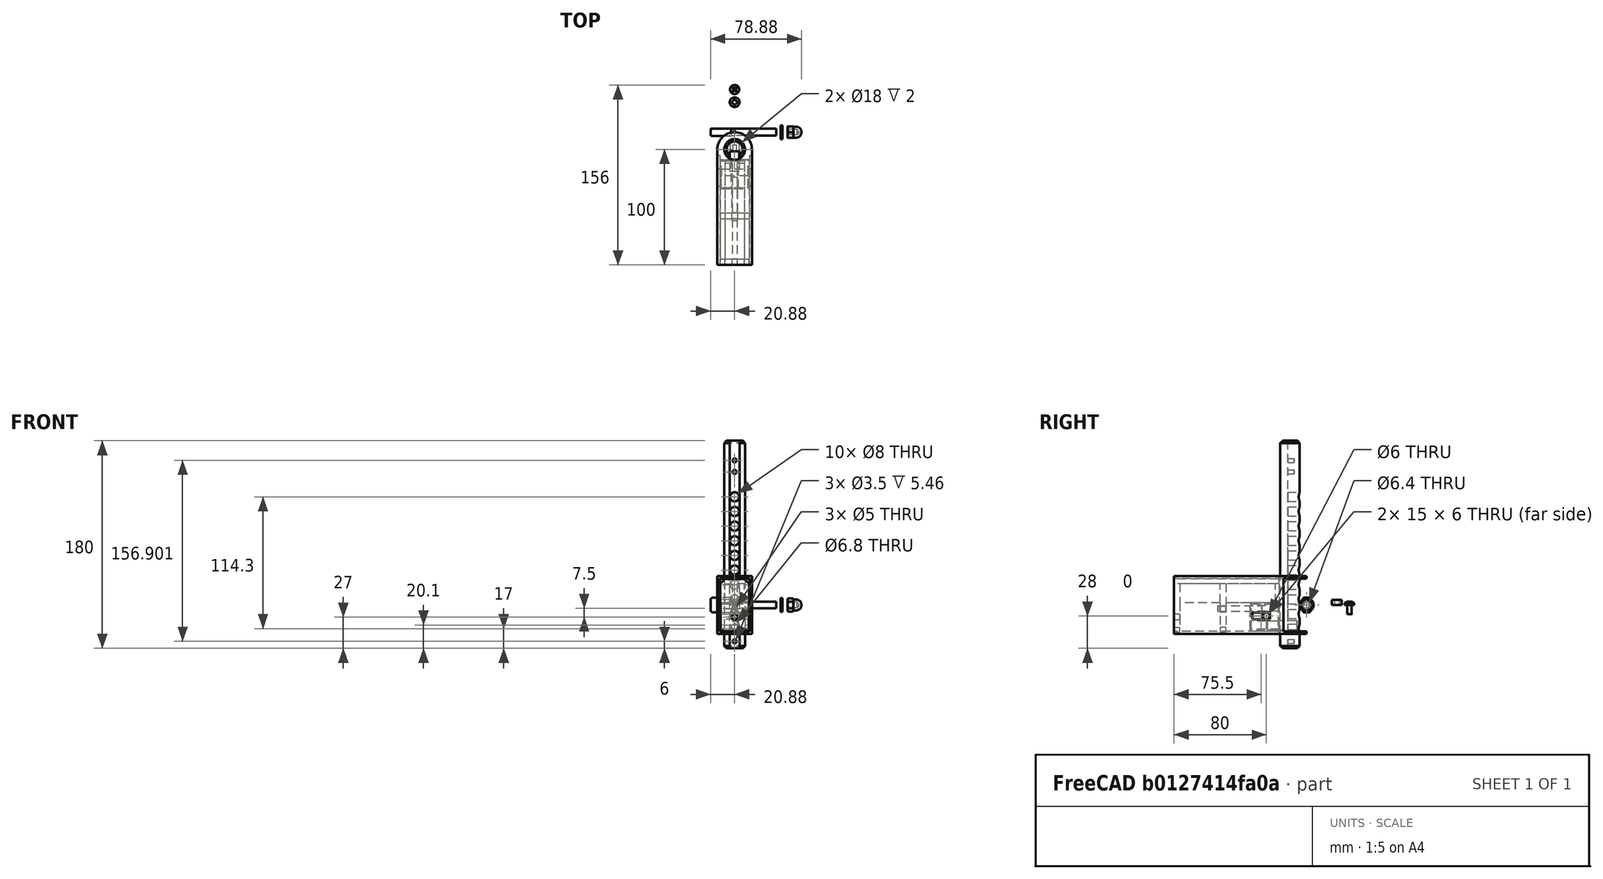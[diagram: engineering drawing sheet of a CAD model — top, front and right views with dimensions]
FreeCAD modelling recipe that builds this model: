
FCSTD DOCUMENT  (FreeCAD 0.20R29603 (Git))
Label: armrest
License: All rights reserved
LicenseURL: http://en.wikipedia.org/wiki/All_rights_reserved
objects: TechDraw::DrawViewDimension×48, Sketcher::SketchObject×21, PartDesign::Pad×13, TechDraw::DrawProjGroupItem×11, PartDesign::Pocket×8, PartDesign::Body×8, TechDraw::DrawProjGroup×6, Part::FeaturePython×3, TechDraw::DrawSVGTemplate×3, TechDraw::DrawViewAnnotation×3, TechDraw::DrawPage×3, PartDesign::Chamfer×2, PartDesign::Fillet×2, App::DocumentObjectGroup×2, Spreadsheet::Sheet×1, PartDesign::Mirrored×1, TechDraw::DrawViewDimExtent×1
note: 83 computed .brp shape members not serialized (recipe doc carries the construction recipe); baked Part::Feature solids carry a one-line shape summary decoded from their .brp

FEATURE [Spreadsheet::Sheet] Spreadsheet  label="data"
  cells = A1=rod_dia; B1(rod_dia)=18; A2=rod_length; B2(rod_length)=180; C2==25.4 * 7.25; A3=rod_angle; B3(rod_angle)=117; A4=rod_holespacing; B4(rod_holespacing)==25.4 / 2; A5=rod_holedia; B5(rod_holedia)=8; A6=rod_slotwidth; B6(rod_slotwidth)=8.4; A7=rod_slotheight; B7(rod_slotheight)=6.5; A8=rod_pindia; B8(rod_pindia)=5; A9=rod_blockerdia; B9(rod_blockerdia)=3.5; A11=body_width; B11(body_width)=30; A12=body_height; B12(body_height)=50; A13=body_walls; B13(body_walls)=2; A14=body_length; B14(body_length)=115; A16=lever_height; B16(lever_height)==25.4 / 2; A17=lever_thickness; B17(lever_thickness)==25.4 / 4; A18=lever_outerLength; B18(lever_outerLength)==25.4 * 0.704; A19=lever_holelength; B19(lever_holelength)==25.4 * 0.848; A20=lever_dia; B20(lever_dia)=6; A22=pin_block_height; B22(pin_block_height)=25; A23=pin_block_width; B23(pin_block_width)=25; A24=pin_block_length; B24(pin_block_length)=25; A25=pin_block_guide_dia; B25(pin_block_guide_dia)=5; A26=pin_block_guide_yDist; B26(pin_block_guide_yDist)=20; A27=pin_movement; B27(pin_movement)=8; A28=pin_length; B28(pin_length)==rod_slotheight + pin_movement + 1; A29=pin_housing_frontwall; B29(pin_housing_frontwall)=4; A31=holder_length; B31(holder_length)==pin_movement + pin_block_length + 13; A32=holder_width; B32(holder_width)==body_width - 2 * body_walls - 1; A33=holder_height; B33(holder_height)==body_height - 2 * body_walls - pin_block_height - 0.5; A34=holder_mid_width; B34(holder_mid_width)=5; A35=holder_backlength; B35(holder_backlength)==body_length - 75; A36=holder_backhole_distY; B36(holder_backhole_distY)=13; A37=holder_back_thickness; B37(holder_back_thickness)=5
FEATURE [Sketcher::SketchObject] Sketch
  FullyConstrained = true
  MapMode = 5
  Support = -> [XY_Plane]
  expr: Constraints[10] = <<data>>.rod_slotheight
  expr: Constraints[11] = <<data>>.rod_dia / 2
  expr: Constraints[9] = <<data>>.rod_slotwidth
  sketch-geometry (4):
    g0: ArcOfCircle CenterX=0 CenterY=0 CenterZ=0 NormalX=0 NormalY=0 NormalZ=1 AngleXU=0 Radius=9 StartAngle=2.05631 EndAngle=7.36846
    g1: LineSegment StartX=-4.2 StartY=7.9599 StartZ=0 EndX=-4.2 EndY=1.4599 EndZ=0
    g2: LineSegment StartX=-4.2 StartY=1.4599 StartZ=0 EndX=4.2 EndY=1.4599 EndZ=0
    g3: LineSegment StartX=4.2 StartY=1.4599 StartZ=0 EndX=4.2 EndY=7.9599 EndZ=0
  constraints (12):
    c: Coincident(g0,g-1)
    c: Coincident(g0,g1)
    c: Coincident(g1,g2)
    c: Horizontal(g2)
    c: Coincident(g2,g3)
    c: Coincident(g3,g0)
    c: Vertical(g3)
    c: Vertical(g1)
    c: Equal(g3,g1)
    c: DistanceX(g2,g2) = 8.4
    c: DistanceY(g3,g3) = 6.5
    c: Radius(g0) = 9
FEATURE [PartDesign::Pad] Pad
  Direction = (0,0,1)
  Length = 180
  Length2 = 10
  Profile = -> Sketch
  ReferenceAxis = -> Sketch [N_Axis]
  Type = 0
  expr: Length = <<data>>.rod_length
FEATURE [PartDesign::Chamfer] Chamfer
  Angle = 45
  Base = -> Pad [Edge4,Edge3]
  BaseFeature = -> Pad
  ChamferType = 0
  FlipDirection = false
  Size = 2
  Size2 = 1
  SupportTransform = false
  UseAllEdges = false
FEATURE [Sketcher::SketchObject] Sketch001
  ExternalGeometry = -> [Chamfer]
  FullyConstrained = true
  MapMode = 5
  Placement = pos=(0,0,0) rot=(1,0,0;1.5708rad)
  Support = -> [XZ_Plane]
  expr: Constraints[1] = <<data>>.rod_holedia
  expr: Constraints[6] = <<data>>.rod_holespacing
  sketch-geometry (19):
    g0: Circle CenterX=0 CenterY=17 CenterZ=0 NormalX=0 NormalY=0 NormalZ=1 AngleXU=0 Radius=4
    g1: Circle CenterX=5.212e-13 CenterY=29.7 CenterZ=0 NormalX=0 NormalY=0 NormalZ=1 AngleXU=0 Radius=4
    g2: LineSegment StartX=0 StartY=17 StartZ=0 EndX=5.212e-13 EndY=29.7 EndZ=0
    g3: Circle CenterX=2.0927e-12 CenterY=42.4 CenterZ=0 NormalX=0 NormalY=0 NormalZ=1 AngleXU=0 Radius=4
    g4: LineSegment StartX=5.212e-13 StartY=29.7 StartZ=0 EndX=2.0927e-12 EndY=42.4 EndZ=0
    g5: Circle CenterX=2.6857e-12 CenterY=55.1 CenterZ=0 NormalX=0 NormalY=0 NormalZ=1 AngleXU=0 Radius=4
    g6: LineSegment StartX=2.0927e-12 StartY=42.4 StartZ=0 EndX=2.6857e-12 EndY=55.1 EndZ=0
    g7: Circle CenterX=3.1983e-12 CenterY=67.8 CenterZ=0 NormalX=0 NormalY=0 NormalZ=1 AngleXU=0 Radius=4
    g8: LineSegment StartX=2.6857e-12 StartY=55.1 StartZ=0 EndX=3.1983e-12 EndY=67.8 EndZ=0
    g9: Circle CenterX=3.7092e-12 CenterY=80.5 CenterZ=0 NormalX=0 NormalY=0 NormalZ=1 AngleXU=0 Radius=4
    g10: LineSegment StartX=3.1983e-12 StartY=67.8 StartZ=0 EndX=3.7092e-12 EndY=80.5 EndZ=0
    g11: Circle CenterX=4.22e-12 CenterY=93.2 CenterZ=0 NormalX=0 NormalY=0 NormalZ=1 AngleXU=0 Radius=4
    g12: LineSegment StartX=3.7092e-12 StartY=80.5 StartZ=0 EndX=4.22e-12 EndY=93.2 EndZ=0
    g13: Circle CenterX=4.731e-12 CenterY=105.9 CenterZ=0 NormalX=0 NormalY=0 NormalZ=1 AngleXU=0 Radius=4
    g14: LineSegment StartX=4.22e-12 StartY=93.2 StartZ=0 EndX=4.731e-12 EndY=105.9 EndZ=0
    g15: Circle CenterX=5.2483e-12 CenterY=118.6 CenterZ=0 NormalX=0 NormalY=0 NormalZ=1 AngleXU=0 Radius=4
    g16: LineSegment StartX=4.731e-12 StartY=105.9 StartZ=0 EndX=5.2483e-12 EndY=118.6 EndZ=0
    g17: Circle CenterX=5.8147e-12 CenterY=131.3 CenterZ=0 NormalX=0 NormalY=0 NormalZ=1 AngleXU=0 Radius=4
    g18: LineSegment StartX=5.2483e-12 StartY=118.6 StartZ=0 EndX=5.8147e-12 EndY=131.3 EndZ=0
  constraints (48):
    c: PointOnObject(g0,g-2)
    c: Diameter(g0) = 8
    c: DistanceY(g-1,g0) = 17
    c: Equal(g0,g1) = 8
    c: Coincident(g0,g2)
    c: Coincident(g1,g2)
    c: Distance(g2) = 12.7
    c: Angle(g2) = 1.5708
    c: Equal(g0,g3) = 8
    c: Coincident(g1,g4)
    c: Coincident(g3,g4)
    c: Equal(g2,g4)
    c: Parallel(g4,g2)
    c: Equal(g0,g5) = 8
    c: Coincident(g3,g6)
    c: Coincident(g5,g6)
    c: Equal(g2,g6)
    c: Parallel(g6,g2)
    c: Equal(g0,g7) = 8
    c: Coincident(g5,g8)
    c: Coincident(g7,g8)
    c: Equal(g2,g8)
    c: Parallel(g8,g2)
    c: Equal(g0,g9) = 8
    c: Coincident(g7,g10)
    c: Coincident(g9,g10)
    c: Equal(g2,g10)
    c: Parallel(g10,g2)
    c: Equal(g0,g11) = 8
    c: Coincident(g9,g12)
    c: Coincident(g11,g12)
    c: Equal(g2,g12)
    c: Parallel(g12,g2)
    c: Equal(g0,g13) = 8
    c: Coincident(g11,g14)
    c: Coincident(g13,g14)
    c: Equal(g2,g14)
    c: Parallel(g14,g2)
    c: Equal(g0,g15) = 8
    c: Coincident(g13,g16)
    c: Coincident(g15,g16)
    c: Equal(g2,g16)
    c: Parallel(g16,g2)
    c: Equal(g0,g17) = 8
    c: Coincident(g15,g18)
    c: Coincident(g17,g18)
    c: Equal(g2,g18)
    c: Parallel(g18,g2)
FEATURE [PartDesign::Pocket] Pocket  label="FixationHoles"
  BaseFeature = -> Chamfer
  Direction = (0,1,2e-16)
  Length = 5
  Length2 = 5
  Midplane = true
  Profile = -> Sketch001
  ReferenceAxis = -> Sketch001 [N_Axis]
  Type = 1
FEATURE [Sketcher::SketchObject] Sketch004
  FullyConstrained = true
  MapMode = 5
  Placement = pos=(0,0,0) rot=(1,0,0;1.5708rad)
  Support = -> [XZ_Plane001]
  expr: Constraints[18] = <<data>>.body_height
  expr: Constraints[19] = <<data>>.body_width
  expr: Constraints[20] = <<data>>.body_walls
  expr: Constraints[21] = <<data>>.body_walls
  sketch-geometry (8):
    g0: LineSegment StartX=-15 StartY=25 StartZ=0 EndX=15 EndY=25 EndZ=0
    g1: LineSegment StartX=15 StartY=25 StartZ=0 EndX=15 EndY=-25 EndZ=0
    g2: LineSegment StartX=15 StartY=-25 StartZ=0 EndX=-15 EndY=-25 EndZ=0
    g3: LineSegment StartX=-15 StartY=-25 StartZ=0 EndX=-15 EndY=25 EndZ=0
    g4: LineSegment StartX=-13 StartY=23 StartZ=0 EndX=13 EndY=23 EndZ=0
    g5: LineSegment StartX=13 StartY=23 StartZ=0 EndX=13 EndY=-23 EndZ=0
    g6: LineSegment StartX=13 StartY=-23 StartZ=0 EndX=-13 EndY=-23 EndZ=0
    g7: LineSegment StartX=-13 StartY=-23 StartZ=0 EndX=-13 EndY=23 EndZ=0
  constraints (22):
    c: Coincident(g0,g1)
    c: Coincident(g1,g2)
    c: Coincident(g2,g3)
    c: Coincident(g3,g0)
    c: Horizontal(g0)
    c: Horizontal(g2)
    c: Vertical(g1)
    c: Vertical(g3)
    c: Coincident(g4,g5)
    c: Coincident(g5,g6)
    c: Coincident(g6,g7)
    c: Coincident(g7,g4)
    c: Horizontal(g4)
    c: Horizontal(g6)
    c: Vertical(g5)
    c: Vertical(g7)
    c: Symmetric(g0,g1,g-1)
    c: Symmetric(g4,g5,g-1)
    c: DistanceY(g3,g3) = 50
    c: DistanceX(g0,g0) = 30
    c: DistanceY(g4,g0) = 2
    c: DistanceX(g4,g0) = 2
FEATURE [PartDesign::Pad] Pad001
  Direction = (0,-1,-2e-16)
  Length = 115
  Length2 = 10
  Placement = pos=(0,0,0) rot=(1,0,0;1.5708rad)
  Profile = -> Sketch004
  ReferenceAxis = -> Sketch004 [N_Axis]
  Type = 0
  expr: Length = <<data>>.body_length
FEATURE [Sketcher::SketchObject] Sketch005
  FullyConstrained = true
  MapMode = 5
  Support = -> [XY_Plane001]
  expr: Constraints[1] = <<data>>.rod_dia
  expr: Constraints[2] = <<data>>.body_width / 2
  sketch-geometry (1):
    g0: Circle CenterX=0 CenterY=-15 CenterZ=0 NormalX=0 NormalY=0 NormalZ=1 AngleXU=0 Radius=9
  constraints (3):
    c: PointOnObject(g0,g-2)
    c: Diameter(g0) = 18
    c: DistanceY(g0,g-1) = 15
FEATURE [PartDesign::Pocket] Pocket003  label="RodHole"
  BaseFeature = -> Pad001
  Direction = (0,0,-1)
  Length = 5
  Length2 = 5
  Midplane = true
  Placement = pos=(0,0,0) rot=(1,0,0;1.5708rad)
  Profile = -> Sketch005
  ReferenceAxis = -> Sketch005 [N_Axis]
  Type = 1
FEATURE [Sketcher::SketchObject] Sketch006
  ExternalGeometry = -> [Pocket003]
  FullyConstrained = true
  MapMode = 5
  Support = -> [XY_Plane001]
  sketch-geometry (4):
    g0: ArcOfCircle CenterX=2.1e-15 CenterY=-15 CenterZ=0 NormalX=0 NormalY=0 NormalZ=1 AngleXU=0 Radius=15 StartAngle=7e-16 EndAngle=3.14159
    g1: LineSegment StartX=-15 StartY=-15 StartZ=0 EndX=-15 EndY=0 EndZ=0
    g2: LineSegment StartX=-15 StartY=0 StartZ=0 EndX=15 EndY=5.6e-15 EndZ=0
    g3: LineSegment StartX=15 StartY=5.6e-15 StartZ=0 EndX=15 EndY=-15 EndZ=0
  constraints (11):
    c: PointOnObject(g0,g-4)
    c: PointOnObject(g0,g-5)
    c: PointOnObject(g-1,g0)
    c: Horizontal(g0,g-3)
    c: Horizontal(g-3,g0)
    c: Coincident(g1,g0)
    c: Coincident(g1,g-4)
    c: Coincident(g1,g2)
    c: Coincident(g2,g-5)
    c: Coincident(g2,g3)
    c: Coincident(g3,g0)
FEATURE [PartDesign::Pocket] Pocket004  label="RoundingCut"
  BaseFeature = -> Pocket003
  Direction = (0,0,-1)
  Length = 5
  Length2 = 5
  Midplane = true
  Placement = pos=(0,0,0) rot=(1,0,0;1.5708rad)
  Profile = -> Sketch006
  ReferenceAxis = -> Sketch006 [N_Axis]
  Type = 1
FEATURE [Sketcher::SketchObject] Sketch007
  ExternalGeometry = -> [Pocket004]
  FullyConstrained = true
  MapMode = 5
  Placement = pos=(0,0,0) rot=(1,0,0;1.5708rad)
  Support = -> [XZ_Plane001]
  sketch-geometry (4):
    g0: LineSegment StartX=-15 StartY=23 StartZ=0 EndX=15 EndY=23 EndZ=0
    g1: LineSegment StartX=15 StartY=23 StartZ=0 EndX=15 EndY=-23 EndZ=0
    g2: LineSegment StartX=15 StartY=-23 StartZ=0 EndX=-15 EndY=-23 EndZ=0
    g3: LineSegment StartX=-15 StartY=-23 StartZ=0 EndX=-15 EndY=23 EndZ=0
  constraints (12):
    c: Coincident(g0,g1)
    c: Coincident(g1,g2)
    c: Coincident(g2,g3)
    c: Coincident(g3,g0)
    c: Horizontal(g0)
    c: Horizontal(g2)
    c: Vertical(g1)
    c: Vertical(g3)
    c: PointOnObject(g0,g-5)
    c: PointOnObject(g1,g-6)
    c: Horizontal(g1,g-4)
    c: Horizontal(g-3,g0)
FEATURE [PartDesign::Pocket] Pocket005  label="FrontCutout"
  BaseFeature = -> Pocket004
  Direction = (0,1,2e-16)
  Length = 20
  Length2 = 5
  Placement = pos=(0,0,0) rot=(1,0,0;1.5708rad)
  Profile = -> Sketch007
  ReferenceAxis = -> Sketch007 [N_Axis]
  Reversed = true
  Type = 0
  expr: Length = <<data>>.rod_dia + 2
FEATURE [Sketcher::SketchObject] Sketch008
  ExternalGeometry = -> [Pocket005]
  FullyConstrained = true
  MapMode = 5
  Placement = pos=(0,0,0) rot=(0.57735,0.57735,0.57735;2.0944rad)
  Support = -> [YZ_Plane001]
  expr: Constraints[8] = <<data>>.lever_dia
  expr: Constraints[9] = <<data>>.pin_movement + <<data>>.lever_dia + 1
  sketch-geometry (4):
    g0: LineSegment StartX=-47 StartY=-6.5 StartZ=0 EndX=-32 EndY=-6.5 EndZ=0
    g1: LineSegment StartX=-32 StartY=-6.5 StartZ=0 EndX=-32 EndY=-12.5 EndZ=0
    g2: LineSegment StartX=-32 StartY=-12.5 StartZ=0 EndX=-47 EndY=-12.5 EndZ=0
    g3: LineSegment StartX=-47 StartY=-12.5 StartZ=0 EndX=-47 EndY=-6.5 EndZ=0
  constraints (12):
    c: Coincident(g0,g1)
    c: Coincident(g2,g3)
    c: Coincident(g3,g0)
    c: Horizontal(g0)
    c: Horizontal(g2)
    c: Vertical(g1)
    c: Vertical(g3)
    c: DistanceX(g1) = -32
    c: DistanceY(g1,g1) = 6
    c: DistanceX(g0,g0) = 15
    c: DistanceY(g0) = -6.5
    c: Coincident(g2,g1)
FEATURE [PartDesign::Pocket] Pocket006  label="LeverHole"
  BaseFeature = -> Pocket005
  Direction = (-1,2e-16,-3e-16)
  Length = 5
  Length2 = 5
  Midplane = true
  Placement = pos=(0,0,0) rot=(1,0,0;1.5708rad)
  Profile = -> Sketch008
  ReferenceAxis = -> Sketch008 [N_Axis]
  Type = 1
FEATURE [PartDesign::Body] Body001  label="Housing"
  Group = -> [Sketch004,Pad001,Sketch005,Pocket003,Sketch006,Pocket004,Sketch007,Pocket005,Sketch008,Pocket006]
  Origin = -> Origin001
  Tip = -> Pocket006
FEATURE [Sketcher::SketchObject] Sketch009
  FullyConstrained = true
  MapMode = 5
  Placement = pos=(0,0,0) rot=(1,0,0;1.5708rad)
  Support = -> [XZ_Plane002]
  expr: Constraints[13] = <<data>>.rod_slotheight / 2
  expr: Constraints[14] = <<data>>.body_walls + 1
  expr: Constraints[15] = <<data>>.lever_height / 2
  expr: Constraints[16] = <<data>>.lever_outerLength
  sketch-geometry (6):
    g0: LineSegment StartX=0 StartY=3.25 StartZ=0 EndX=-3 EndY=3.25 EndZ=0
    g1: LineSegment StartX=-3 StartY=3.25 StartZ=0 EndX=-3 EndY=6.35 EndZ=0
    g2: LineSegment StartX=-3 StartY=6.35 StartZ=0 EndX=-20.8816 EndY=6.35 EndZ=0
    g3: LineSegment StartX=-20.8816 StartY=6.35 StartZ=0 EndX=-20.8816 EndY=0 EndZ=0
    g4: LineSegment StartX=-20.8816 StartY=0 StartZ=0 EndX=0 EndY=0 EndZ=0
    g5: LineSegment StartX=0 StartY=0 StartZ=0 EndX=0 EndY=3.25 EndZ=0
  constraints (17):
    c: PointOnObject(g0,g-2)
    c: Coincident(g0,g1)
    c: Vertical(g1)
    c: Coincident(g1,g2)
    c: Coincident(g2,g3)
    c: Vertical(g3)
    c: Coincident(g3,g4)
    c: Coincident(g4,g-1)
    c: Horizontal(g4)
    c: Coincident(g4,g5)
    c: Coincident(g5,g0)
    c: Horizontal(g2)
    c: Horizontal(g0)
    c: DistanceY(g5,g5) = 3.25
    c: DistanceX(g0,g0) = 3
    c: DistanceY(g3,g3) = 6.35
    c: DistanceX(g2,g2) = 17.8816
FEATURE [PartDesign::Pad] Pad002
  Direction = (0,-1,-2e-16)
  Length = 6.35
  Length2 = 10
  Midplane = true
  Placement = pos=(0,0,0) rot=(1,0,0;1.5708rad)
  Profile = -> Sketch009
  ReferenceAxis = -> Sketch009 [N_Axis]
  Type = 0
  expr: Length = <<data>>.lever_thickness
FEATURE [PartDesign::Mirrored] Mirrored
  BaseFeature = -> Pad002
  MirrorPlane = -> Sketch009 [H_Axis]
  Originals = -> [Pad002]
  Placement = pos=(0,0,0) rot=(1,0,0;1.5708rad)
  Refine = true
FEATURE [PartDesign::Fillet] Fillet001
  Base = -> Mirrored [Edge20,Edge8]
  BaseFeature = -> Mirrored
  Placement = pos=(0,0,0) rot=(1,0,0;1.5708rad)
  Radius = 2
  SupportTransform = false
  UseAllEdges = false
FEATURE [PartDesign::Fillet] Fillet002
  Base = -> Fillet001 [Edge1,Edge4]
  BaseFeature = -> Fillet001
  Placement = pos=(0,0,0) rot=(1,0,0;1.5708rad)
  Radius = 1
  SupportTransform = false
  UseAllEdges = false
FEATURE [Sketcher::SketchObject] Sketch010
  FullyConstrained = true
  MapMode = 5
  Placement = pos=(0,0,0) rot=(0.57735,0.57735,0.57735;2.0944rad)
  Support = -> [YZ_Plane002]
  expr: Constraints[1] = <<data>>.lever_dia
  sketch-geometry (1):
    g0: Circle CenterX=0 CenterY=0 CenterZ=0 NormalX=0 NormalY=0 NormalZ=1 AngleXU=0 Radius=3
  constraints (2):
    c: Coincident(g0,g-1)
    c: Diameter(g0) = 6
FEATURE [PartDesign::Pad] Pad003
  BaseFeature = -> Fillet002
  Direction = (1,-2e-16,3e-16)
  Length = 36
  Length2 = 10
  Placement = pos=(0,0,0) rot=(1,0,0;1.5708rad)
  Profile = -> Sketch010
  ReferenceAxis = -> Sketch010 [N_Axis]
  Type = 0
  expr: Length = <<data>>.body_width + 6
FEATURE [PartDesign::Body] Body002  label="Lever"
  Group = -> [Sketch009,Pad002,Mirrored,Fillet001,Fillet002,Sketch010,Pad003]
  Origin = -> Origin002
  Tip = -> Pad003
FEATURE [Part::FeaturePython] Nut  label="M6-Nut"  # Fasteners workbench fastener (typed FeaturePython)
  Placement = pos=(46,0,0) rot=(0,1,0;1.5708rad)
  diameter = 3
  invert = false
  leftHanded = false
  matchOuter = false
  offset = 0
  thread = false
  type = 9
FEATURE [Part::FeaturePython] Washer  label="M6-Washer"  # Fasteners workbench fastener (typed FeaturePython)
  Placement = pos=(40,0,1e-15) rot=(0,1,0;1.5708rad)
  diameter = 7
  invert = false
  matchOuter = false
  offset = 0
  type = 5
FEATURE [Sketcher::SketchObject] Sketch011
  FullyConstrained = true
  MapMode = 5
  Support = -> [XY_Plane003]
  expr: Constraints[3] = <<data>>.rod_slotwidth
  sketch-geometry (2):
    g0: Circle CenterX=0 CenterY=0 CenterZ=0 NormalX=0 NormalY=0 NormalZ=1 AngleXU=0 Radius=4.2
    g1: Circle CenterX=0 CenterY=0 CenterZ=0 NormalX=0 NormalY=0 NormalZ=1 AngleXU=0 Radius=2
  constraints (4):
    c: Coincident(g0,g-1)
    c: Coincident(g1,g0)
    c: Diameter(g1) = 4
    c: Diameter(g0) = 8.4
FEATURE [PartDesign::Pad] Pad004
  Direction = (0,0,1)
  Length = 4.5
  Length2 = 10
  Profile = -> Sketch011
  ReferenceAxis = -> Sketch011 [N_Axis]
  Type = 0
  expr: Length = <<data>>.rod_slotheight - 2
FEATURE [PartDesign::Body] Body003  label="RodBlocker"
  Group = -> [Sketch011,Pad004]
  Origin = -> Origin003
  Placement = pos=(0,26,0) rot=(0,0,1;0rad)
  Tip = -> Pad004
FEATURE [Part::FeaturePython] Screw  label="M4x8-Screw"  # Fasteners workbench fastener (typed FeaturePython)
  Placement = pos=(0,37,0) rot=(0,0,1;0rad)
  diameter = 6
  invert = false
  leftHanded = false
  length = 2
  lengthCustom = 8
  matchOuter = false
  offset = 0
  thread = false
  type = 49
FEATURE [Sketcher::SketchObject] Sketch012
  FullyConstrained = true
  MapMode = 5
  Placement = pos=(0,0,0) rot=(1,0,0;1.5708rad)
  Support = -> [XZ_Plane004]
  expr: Constraints[1] = <<data>>.rod_holedia
  sketch-geometry (1):
    g0: Circle CenterX=0 CenterY=0 CenterZ=0 NormalX=0 NormalY=0 NormalZ=1 AngleXU=0 Radius=4
  constraints (2):
    c: Coincident(g0,g-1)
    c: Diameter(g0) = 8
FEATURE [PartDesign::Pad] Pad005  label="frontBlockingPart"
  Direction = (0,-1,-2e-16)
  Length = 15.5
  Length2 = 10
  Placement = pos=(0,0,0) rot=(1,0,0;1.5708rad)
  Profile = -> Sketch012
  ReferenceAxis = -> Sketch012 [N_Axis]
  Reversed = true
  Type = 0
  expr: Length = <<data>>.pin_length
FEATURE [Sketcher::SketchObject] Sketch013
  FullyConstrained = true
  MapMode = 5
  Placement = pos=(0,0,0) rot=(1,0,0;1.5708rad)
  Support = -> [XZ_Plane004]
  sketch-geometry (1):
    g0: Circle CenterX=0 CenterY=0 CenterZ=0 NormalX=0 NormalY=0 NormalZ=1 AngleXU=0 Radius=3.925
  constraints (2):
    c: Coincident(g0,g-1)
    c: Diameter(g0) = 7.85
FEATURE [PartDesign::Pad] Pad006  label="backThreadedPart"
  BaseFeature = -> Pad005
  Direction = (0,-1,-2e-16)
  Length = 10
  Length2 = 10
  Placement = pos=(0,0,0) rot=(1,0,0;1.5708rad)
  Profile = -> Sketch013
  ReferenceAxis = -> Sketch013 [N_Axis]
  Type = 0
FEATURE [PartDesign::Body] Body004  label="LockingPin"
  Group = -> [Sketch012,Pad005,Sketch013,Pad006]
  Origin = -> Origin004
  Placement = pos=(0,-24,-17.5) rot=(0,0,1;0rad)
  Tip = -> Pad006
FEATURE [Sketcher::SketchObject] Sketch014
  FullyConstrained = true
  MapMode = 5
  Placement = pos=(0,0,0) rot=(0.57735,0.57735,0.57735;2.0944rad)
  Support = -> [YZ_Plane005]
  expr: Constraints[16] = <<data>>.rod_holedia
  expr: Constraints[22] = <<data>>.lever_dia
  expr: Constraints[24] = <<data>>.pin_block_height / 2 + 1
  expr: Constraints[8] = <<data>>.pin_block_length
  expr: Constraints[9] = <<data>>.pin_block_height
  sketch-geometry (8):
    g0: LineSegment StartX=-12.5 StartY=12.5 StartZ=0 EndX=12.5 EndY=12.5 EndZ=0
    g1: LineSegment StartX=12.5 StartY=12.5 StartZ=0 EndX=12.5 EndY=-12.5 EndZ=0
    g2: LineSegment StartX=12.5 StartY=-12.5 StartZ=0 EndX=-12.5 EndY=-12.5 EndZ=0
    g3: LineSegment StartX=-12.5 StartY=-12.5 StartZ=0 EndX=-12.5 EndY=12.5 EndZ=0
    g4: LineSegment StartX=-12.5 StartY=9 StartZ=0 EndX=12.5 EndY=9 EndZ=0
    g5: LineSegment StartX=-12.5 StartY=1 StartZ=0 EndX=12.5 EndY=1 EndZ=0
    g6: LineSegment StartX=-12.5 StartY=1 StartZ=0 EndX=12.5 EndY=1 EndZ=0
    g7: Circle CenterX=1.5 CenterY=1 CenterZ=0 NormalX=0 NormalY=0 NormalZ=1 AngleXU=0 Radius=3
  constraints (26):
    c: Coincident(g0,g1)
    c: Coincident(g1,g2)
    c: Coincident(g2,g3)
    c: Coincident(g3,g0)
    c: Horizontal(g0)
    c: Horizontal(g2)
    c: Vertical(g1)
    c: Vertical(g3)
    c: DistanceX(g0,g0) = 25
    c: DistanceY(g3,g3) = 25
    c: PointOnObject(g4,g3)
    c: PointOnObject(g4,g1)
    c: Horizontal(g4)
    c: PointOnObject(g5,g3)
    c: PointOnObject(g5,g1)
    c: Horizontal(g5)
    c: DistanceY(g5,g4) = 8
    c: DistanceY(g4,g0) = 3.5
    c: PointOnObject(g6,g3)
    c: PointOnObject(g6,g1)
    c: Horizontal(g6)
    c: PointOnObject(g7,g6)
    c: Diameter(g7) = 6
    c: Symmetric(g0,g1,g-1)
    c: DistanceY(g1,g6) = 13.5
    c: DistanceX(g7,g1) = 11
FEATURE [PartDesign::Pad] Pad007
  Direction = (1,-2e-16,3e-16)
  Length = 25
  Length2 = 10
  Midplane = true
  Placement = pos=(0,0,0) rot=(0.57735,0.57735,0.57735;2.0944rad)
  Profile = -> Sketch014
  ReferenceAxis = -> Sketch014 [N_Axis]
  Type = 0
  expr: Length = <<data>>.pin_block_width
FEATURE [Sketcher::SketchObject] Sketch015
  ExternalGeometry = -> [Pad007]
  FullyConstrained = true
  MapMode = 5
  Placement = pos=(0,0,0) rot=(1,0,0;1.5708rad)
  Support = -> [XZ_Plane005]
  sketch-geometry (2):
    g0: Circle CenterX=0 CenterY=-6.9 CenterZ=0 NormalX=0 NormalY=0 NormalZ=1 AngleXU=0 Radius=3.4
    g1: LineSegment StartX=-12.5 StartY=-3.5 StartZ=0 EndX=12.5 EndY=-3.5 EndZ=0
  constraints (7):
    c: PointOnObject(g0,g-2)
    c: Diameter(g0) = 6.8
    c: PointOnObject(g1,g-4)
    c: PointOnObject(g1,g-5)
    c: Horizontal(g1)
    c: Tangent(g0,g1)
    c: DistanceY(g-4,g1) = 9
FEATURE [PartDesign::Pocket] Pocket007  label="M8ThtroughHole"
  BaseFeature = -> Pad007
  Direction = (0,1,2e-16)
  Length = 5
  Length2 = 5
  Midplane = true
  Placement = pos=(0,0,0) rot=(0.57735,0.57735,0.57735;2.0944rad)
  Profile = -> Sketch015
  ReferenceAxis = -> Sketch015 [N_Axis]
  Type = 1
FEATURE [PartDesign::Chamfer] Chamfer001
  Angle = 45
  Base = -> Pocket007 [Face4,Face5,Face1,Face6]
  BaseFeature = -> Pocket007
  ChamferType = 0
  FlipDirection = false
  Placement = pos=(0,0,0) rot=(0.57735,0.57735,0.57735;2.0944rad)
  Size = 1
  Size2 = 1
  SupportTransform = false
  UseAllEdges = false
FEATURE [Sketcher::SketchObject] Sketch016
  FullyConstrained = false
  MapMode = 5
  Placement = pos=(0,0,0) rot=(1,0,0;1.5708rad)
  Support = -> [XZ_Plane]
  expr: Constraints[5] = <<data>>.rod_blockerdia
  sketch-geometry (3):
    g0: Circle CenterX=0 CenterY=162.901 CenterZ=0 NormalX=0 NormalY=0 NormalZ=1 AngleXU=0 Radius=1.75
    g1: Circle CenterX=0 CenterY=152.901 CenterZ=0 NormalX=0 NormalY=0 NormalZ=1 AngleXU=0 Radius=1.75
    g2: Circle CenterX=0 CenterY=6 CenterZ=0 NormalX=0 NormalY=0 NormalZ=1 AngleXU=0 Radius=1.75
  constraints (8):
    c: PointOnObject(g0,g-2)
    c: PointOnObject(g1,g-2)
    c: PointOnObject(g2,g-2)
    c: Equal(g0,g1)
    c: Equal(g0,g2)
    c: Diameter(g0) = 3.5
    c: DistanceY(g2) = 6
    c: DistanceY(g1,g0) = 10
FEATURE [PartDesign::Pocket] Pocket008
  BaseFeature = -> Pocket
  Direction = (0,1,2e-16)
  Length = 8
  Length2 = 5
  Midplane = true
  Profile = -> Sketch016
  ReferenceAxis = -> Sketch016 [N_Axis]
  Type = 0
FEATURE [PartDesign::Body] Body  label="Rod"
  Group = -> [Sketch,Pad,Chamfer,Sketch001,Pocket,Sketch016,Pocket008]
  Origin = -> Origin
  Placement = pos=(0,-15,-37.5) rot=(0,0,1;3.14159rad)
  Tip = -> Pocket008
FEATURE [App::DocumentObjectGroup] Group001  label="RodParts"
  Group = -> [Body,Body003,Screw]
FEATURE [Sketcher::SketchObject] Sketch017
  FullyConstrained = true
  MapMode = 5
  Placement = pos=(0,0,0) rot=(1,0,0;1.5708rad)
  Support = -> [XZ_Plane006]
  expr: Constraints[10] = <<data>>.holder_height
  expr: Constraints[8] = <<data>>.holder_width
  sketch-geometry (6):
    g0: LineSegment StartX=12.5 StartY=2 StartZ=0 EndX=-12.5 EndY=2 EndZ=0
    g1: LineSegment StartX=-12.5 StartY=2 StartZ=0 EndX=-12.5 EndY=18.5 EndZ=0
    g2: LineSegment StartX=-12.5 StartY=18.5 StartZ=0 EndX=-8.5 EndY=22.5 EndZ=0
    g3: LineSegment StartX=-8.5 StartY=22.5 StartZ=0 EndX=8.5 EndY=22.5 EndZ=0
    g4: LineSegment StartX=8.5 StartY=22.5 StartZ=0 EndX=12.5 EndY=18.5 EndZ=0
    g5: LineSegment StartX=12.5 StartY=18.5 StartZ=0 EndX=12.5 EndY=2 EndZ=0
  constraints (16):
    c: Coincident(g0,g1)
    c: Vertical(g1)
    c: Coincident(g1,g2)
    c: Coincident(g2,g3)
    c: Coincident(g3,g4)
    c: Coincident(g4,g5)
    c: Coincident(g5,g0)
    c: Vertical(g5)
    c: DistanceX(g0,g0) = 25
    c: Symmetric(g0,g0,g-2)
    c: DistanceY(g0,g2) = 20.5
    c: Symmetric(g2,g3,g-2)
    c: Horizontal(g4,g1)
    c: DistanceY(g1,g2) = 4
    c: DistanceX(g1,g2) = 4
    c: DistanceY(g0) = 2
FEATURE [PartDesign::Pad] Pad008  label="Pad008_front"
  Direction = (0,-1,-2e-16)
  Length = 3
  Length2 = 10
  Placement = pos=(0,0,0) rot=(1,0,0;1.5708rad)
  Profile = -> Sketch017
  ReferenceAxis = -> Sketch017 [N_Axis]
  Type = 0
FEATURE [Sketcher::SketchObject] Sketch018
  ExternalGeometry = -> [Pad008]
  FullyConstrained = true
  MapMode = 5
  Placement = pos=(0,0,0) rot=(1,0,0;1.5708rad)
  Support = -> [XZ_Plane006]
  sketch-geometry (14):
    g0: LineSegment StartX=-12.5 StartY=2 StartZ=0 EndX=-12.5 EndY=18.5 EndZ=0
    g1: LineSegment StartX=-12.5 StartY=18.5 StartZ=0 EndX=-8.5 EndY=22.5 EndZ=0
    g2: LineSegment StartX=-8.5 StartY=22.5 StartZ=0 EndX=8.5 EndY=22.5 EndZ=0
    g3: LineSegment StartX=8.5 StartY=22.5 StartZ=0 EndX=12.5 EndY=18.5 EndZ=0
    g4: LineSegment StartX=12.5 StartY=18.5 StartZ=0 EndX=12.5 EndY=2 EndZ=0
    g5: LineSegment StartX=12.5 StartY=2 StartZ=0 EndX=8.5 EndY=2 EndZ=0
    g6: LineSegment StartX=8.5 StartY=2 StartZ=0 EndX=8.5 EndY=18.5 EndZ=0
    g7: LineSegment StartX=8.5 StartY=18.5 StartZ=0 EndX=2 EndY=18.5 EndZ=0
    g8: LineSegment StartX=2 StartY=18.5 StartZ=0 EndX=2 EndY=2 EndZ=0
    g9: LineSegment StartX=2 StartY=2 StartZ=0 EndX=-2 EndY=2 EndZ=0
    g10: LineSegment StartX=-2 StartY=2 StartZ=0 EndX=-2 EndY=18.5 EndZ=0
    g11: LineSegment StartX=-2 StartY=18.5 StartZ=0 EndX=-8.5 EndY=18.5 EndZ=0
    g12: LineSegment StartX=-8.5 StartY=18.5 StartZ=0 EndX=-8.5 EndY=2 EndZ=0
    g13: LineSegment StartX=-8.5 StartY=2 StartZ=0 EndX=-12.5 EndY=2 EndZ=0
  constraints (36):
    c: Coincident(g-4,g0)
    c: Coincident(g0,g-5)
    c: Coincident(g0,g1)
    c: Coincident(g1,g-5)
    c: Coincident(g1,g2)
    c: Coincident(g2,g-6)
    c: Coincident(g2,g3)
    c: Coincident(g3,g-6)
    c: Coincident(g3,g4)
    c: Coincident(g4,g-4)
    c: Coincident(g4,g5)
    c: PointOnObject(g5,g-4)
    c: Coincident(g5,g6)
    c: Vertical(g6)
    c: Coincident(g6,g7)
    c: Horizontal(g7)
    c: Coincident(g7,g8)
    c: PointOnObject(g8,g-4)
    c: Vertical(g8)
    c: Coincident(g8,g9)
    c: PointOnObject(g9,g-4)
    c: Coincident(g9,g10)
    c: Vertical(g10)
    c: Coincident(g10,g11)
    c: Horizontal(g11)
    c: Coincident(g11,g12)
    c: PointOnObject(g12,g-4)
    c: Vertical(g12)
    c: Coincident(g12,g13)
    c: Coincident(g13,g0)
    c: Equal(g11,g7)
    c: Equal(g5,g9)
    c: Equal(g9,g13)
    c: DistanceX(g13,g13) = 4
    c: Horizontal(g0,g11)
    c: Horizontal(g11,g7)
FEATURE [PartDesign::Pad] Pad009  label="Pad009_topRails"
  BaseFeature = -> Pad008
  Direction = (0,-1,-2e-16)
  Length = 91
  Length2 = 10
  Placement = pos=(0,0,0) rot=(1,0,0;1.5708rad)
  Profile = -> Sketch018
  ReferenceAxis = -> Sketch018 [N_Axis]
  Type = 0
  expr: Length = <<data>>.holder_length + <<data>>.holder_mid_width + <<data>>.holder_backlength
FEATURE [Sketcher::SketchObject] Sketch019
  AttachmentOffset = pos=(0,0,46) rot=(0,0,1;0rad)
  ExternalGeometry = -> [Pad009]
  FullyConstrained = true
  MapMode = 5
  Placement = pos=(0,-46,-1.02e-14) rot=(1,0,0;1.5708rad)
  Support = -> [XZ_Plane006]
  expr: .AttachmentOffset.Base.z = <<data>>.holder_length
  expr: Constraints[15] = <<data>>.body_height - 2 * <<data>>.body_walls
  expr: Constraints[26] = <<data>>.pin_block_guide_yDist
  expr: Constraints[27] = <<data>>.pin_block_guide_dia
  sketch-geometry (11):
    g0: LineSegment StartX=-12.5 StartY=18.5 StartZ=0 EndX=-12.5 EndY=-19.5 EndZ=0
    g1: LineSegment StartX=-12.5 StartY=-19.5 StartZ=0 EndX=-8.5 EndY=-23.5 EndZ=0
    g2: LineSegment StartX=-8.5 StartY=-23.5 StartZ=0 EndX=8.5 EndY=-23.5 EndZ=0
    g3: LineSegment StartX=8.5 StartY=-23.5 StartZ=0 EndX=12.5 EndY=-19.5 EndZ=0
    g4: LineSegment StartX=12.5 StartY=-19.5 StartZ=0 EndX=12.5 EndY=18.5 EndZ=0
    g5: LineSegment StartX=12.5 StartY=18.5 StartZ=0 EndX=8.5 EndY=22.5 EndZ=0
    g6: LineSegment StartX=8.5 StartY=22.5 StartZ=0 EndX=-8.5 EndY=22.5 EndZ=0
    g7: LineSegment StartX=-8.5 StartY=22.5 StartZ=0 EndX=-12.5 EndY=18.5 EndZ=0
    g8: LineSegment StartX=-8.5 StartY=-23.5 StartZ=0 EndX=-12.5 EndY=-23.5 EndZ=0
    g9: LineSegment StartX=-12.5 StartY=-23.5 StartZ=0 EndX=-12.5 EndY=-19.5 EndZ=0
    g10: Circle CenterX=0 CenterY=-3.5 CenterZ=0 NormalX=0 NormalY=0 NormalZ=1 AngleXU=0 Radius=2.5
  constraints (28):
    c: Coincident(g-3,g0)
    c: Vertical(g0)
    c: Coincident(g0,g1)
    c: Coincident(g1,g2)
    c: Horizontal(g2)
    c: Coincident(g2,g3)
    c: Coincident(g3,g4)
    c: Coincident(g4,g-4)
    c: Vertical(g4)
    c: Coincident(g4,g5)
    c: Coincident(g5,g-4)
    c: Coincident(g5,g6)
    c: Coincident(g6,g-3)
    c: Coincident(g6,g7)
    c: Coincident(g7,g0)
    c: DistanceY(g1,g6) = 46
    c: Vertical(g1,g6)
    c: Vertical(g2,g5)
    c: Horizontal(g3,g0)
    c: Coincident(g1,g8)
    c: Horizontal(g8)
    c: Coincident(g8,g9)
    c: Coincident(g9,g0)
    c: Vertical(g9)
    c: Equal(g9,g8)
    c: PointOnObject(g10,g-2)
    c: DistanceY(g2,g10) = 20
    c: Diameter(g10) = 5
FEATURE [PartDesign::Pad] Pad010  label="Pad010_mid"
  BaseFeature = -> Pad009
  Direction = (0,-1,-2e-16)
  Length = 5
  Length2 = 10
  Placement = pos=(0,0,0) rot=(1,0,0;1.5708rad)
  Profile = -> Sketch019
  ReferenceAxis = -> Sketch019 [N_Axis]
  Type = 0
FEATURE [Sketcher::SketchObject] Sketch020
  ExternalGeometry = -> [Chamfer001]
  FullyConstrained = true
  MapMode = 5
  Placement = pos=(0,0,0) rot=(1,0,0;1.5708rad)
  Support = -> [XZ_Plane005]
  expr: Constraints[1] = <<data>>.pin_block_guide_dia
  expr: Constraints[2] = <<data>>.pin_block_guide_yDist
  sketch-geometry (1):
    g0: Circle CenterX=0 CenterY=7.5 CenterZ=0 NormalX=0 NormalY=0 NormalZ=1 AngleXU=0 Radius=2.5
  constraints (3):
    c: PointOnObject(g0,g-2)
    c: Diameter(g0) = 5
    c: DistanceY(g-3,g0) = 20
FEATURE [PartDesign::Pocket] Pocket009
  BaseFeature = -> Chamfer001
  Direction = (0,1,2e-16)
  Length = 5
  Length2 = 5
  Midplane = true
  Placement = pos=(0,0,0) rot=(0.57735,0.57735,0.57735;2.0944rad)
  Profile = -> Sketch020
  ReferenceAxis = -> Sketch020 [N_Axis]
  Type = 1
FEATURE [PartDesign::Body] Body005  label="PinBlock"
  Group = -> [Sketch014,Pad007,Sketch015,Pocket007,Chamfer001,Sketch020,Pocket009]
  Origin = -> Origin005
  Placement = pos=(0,-36.5,-10.5) rot=(0,0,1;0rad)
  Tip = -> Pocket009
FEATURE [App::DocumentObjectGroup] Group  label="LeverParts"
  Group = -> [Body002,Nut,Washer,Body004,Body005]
FEATURE [Sketcher::SketchObject] Sketch021
  AttachmentOffset = pos=(0,0,91) rot=(0,0,1;0rad)
  ExternalGeometry = -> [Pad010]
  FullyConstrained = true
  MapMode = 5
  Placement = pos=(0,-91,-2.02e-14) rot=(1,0,0;1.5708rad)
  Support = -> [XZ_Plane006]
  expr: .AttachmentOffset.Base.z = <<data>>.holder_length + <<data>>.holder_mid_width + <<data>>.holder_backlength
  expr: Constraints[18] = <<data>>.holder_backhole_distY
  sketch-geometry (9):
    g0: LineSegment StartX=-8.5 StartY=22.5 StartZ=0 EndX=-12.5 EndY=18.5 EndZ=0
    g1: LineSegment StartX=-12.5 StartY=18.5 StartZ=0 EndX=-12.5 EndY=-19.5 EndZ=0
    g2: LineSegment StartX=-12.5 StartY=-19.5 StartZ=0 EndX=-8.5 EndY=-23.5 EndZ=0
    g3: LineSegment StartX=-8.5 StartY=-23.5 StartZ=0 EndX=8.5 EndY=-23.5 EndZ=0
    g4: LineSegment StartX=8.5 StartY=-23.5 StartZ=0 EndX=12.5 EndY=-19.5 EndZ=0
    g5: LineSegment StartX=12.5 StartY=-19.5 StartZ=0 EndX=12.5 EndY=18.5 EndZ=0
    g6: LineSegment StartX=12.5 StartY=18.5 StartZ=0 EndX=8.5 EndY=22.5 EndZ=0
    g7: LineSegment StartX=8.5 StartY=22.5 StartZ=0 EndX=-8.5 EndY=22.5 EndZ=0
    g8: Circle CenterX=0 CenterY=-10.5 CenterZ=0 NormalX=0 NormalY=0 NormalZ=1 AngleXU=0 Radius=2.5
  constraints (19):
    c: Coincident(g-4,g0)
    c: Coincident(g0,g-8)
    c: Coincident(g0,g1)
    c: Coincident(g1,g-5)
    c: Coincident(g1,g2)
    c: Coincident(g2,g-3)
    c: Coincident(g2,g3)
    c: Coincident(g3,g-3)
    c: Coincident(g3,g4)
    c: Coincident(g4,g-6)
    c: Coincident(g4,g5)
    c: Coincident(g5,g-7)
    c: Coincident(g5,g6)
    c: Coincident(g6,g-4)
    c: Coincident(g6,g7)
    c: Coincident(g7,g0)
    c: PointOnObject(g8,g-2)
    c: Diameter(g8) = 5
    c: DistanceY(g3,g8) = 13
FEATURE [PartDesign::Pad] Pad011
  BaseFeature = -> Pad010
  Direction = (0,-1,-2e-16)
  Length = 5
  Length2 = 10
  Placement = pos=(0,0,0) rot=(1,0,0;1.5708rad)
  Profile = -> Sketch021
  ReferenceAxis = -> Sketch021 [N_Axis]
  Refine = true
  Reversed = true
  Type = 0
  expr: Length = <<data>>.holder_back_thickness
FEATURE [PartDesign::Body] Body006  label="Holder"
  Group = -> [Sketch017,Pad008,Sketch018,Pad009,Sketch019,Pad010,Sketch021,Pad011]
  Origin = -> Origin006
  Placement = pos=(0,-24,0) rot=(0,0,1;0rad)
  Tip = -> Pad011
FEATURE [Sketcher::SketchObject] Sketch022
  FullyConstrained = true
  MapMode = 5
  Placement = pos=(0,0,0) rot=(1,0,0;1.5708rad)
  Support = -> [XZ_Plane007]
  expr: Constraints[1] = <<data>>.pin_block_guide_dia
  sketch-geometry (1):
    g0: Circle CenterX=0 CenterY=0 CenterZ=0 NormalX=0 NormalY=0 NormalZ=1 AngleXU=0 Radius=2.5
  constraints (2):
    c: Coincident(g0,g-1)
    c: Diameter(g0) = 5
FEATURE [PartDesign::Pad] Pad012
  Direction = (0,-1,-2e-16)
  Length = 38
  Length2 = 10
  Placement = pos=(0,0,0) rot=(1,0,0;1.5708rad)
  Profile = -> Sketch022
  ReferenceAxis = -> Sketch022 [N_Axis]
  Type = 0
FEATURE [PartDesign::Body] Body007  label="GuidePin"
  Group = -> [Sketch022,Pad012]
  Origin = -> Origin007
  Placement = pos=(0,-39,-3) rot=(0,0,1;0rad)
  Tip = -> Pad012
FEATURE [TechDraw::DrawSVGTemplate] Template
  Height = 210
  Orientation = 1
  Width = 297
FEATURE [TechDraw::DrawProjGroupItem] ProjItem  label="Front"
  CoarseView = false
  Direction = (-1,0,0)
  Focus = 100
  HardHidden = false
  IsoCount = 0
  IsoHidden = false
  IsoVisible = false
  LockPosition = true
  Perspective = false
  Rotation = 0
  RotationVector = (0,-1,0)
  ScaleType = 2
  SeamHidden = false
  SeamVisible = true
  SmoothHidden = false
  SmoothVisible = true
  Source = -> [Body001]
  Type = 0
  X = 0
  XDirection = (0,-1,0)
  Y = 0
FEATURE [TechDraw::DrawProjGroupItem] ProjItem002  label="Bottom"
  CoarseView = false
  Direction = (0,0,-1)
  Focus = 100
  HardHidden = false
  IsoCount = 0
  IsoHidden = false
  IsoVisible = false
  LockPosition = false
  Perspective = false
  Rotation = 0
  RotationVector = (1,0,0)
  ScaleType = 2
  SeamHidden = false
  SeamVisible = true
  SmoothHidden = false
  SmoothVisible = true
  Source = -> [Body001]
  Type = 5
  X = 0
  XDirection = (0,-1,0)
  Y = 65
FEATURE [TechDraw::DrawProjGroup] ProjGroup
  Anchor = -> ProjItem
  AutoDistribute = true
  LockPosition = false
  ProjectionType = 0
  Rotation = 0
  ScaleType = 0
  Source = -> [Body001]
  Views = -> [ProjItem,ProjItem002]
  X = 105.3
  Y = 84.3509
  spacingX = 15
  spacingY = 15
FEATURE [TechDraw::DrawViewDimension] Dimension
  AngleOverride = false
  Arbitrary = false
  ArbitraryTolerances = false
  EqualTolerance = true
  ExtensionAngle = 0
  FormatSpec = ⌀%.2w
  FormatSpecOverTolerance = %+.2w
  FormatSpecUnderTolerance = %+.2w
  Inverted = false
  LineAngle = 0
  LockPosition = false
  MeasureType = 1
  OverTolerance = 0
  References2D = -> [ProjItem002]
  Rotation = 0
  ScaleType = 0
  TheoreticalExact = false
  Type = 5
  UnderTolerance = 0
  X = -11.683
  Y = 26.6264
FEATURE [TechDraw::DrawViewDimension] Dimension001
  AngleOverride = false
  Arbitrary = false
  ArbitraryTolerances = false
  EqualTolerance = true
  ExtensionAngle = 0
  FormatSpec = ⌀%.2w
  FormatSpecOverTolerance = %+.2w
  FormatSpecUnderTolerance = %+.2w
  Inverted = false
  LineAngle = 0
  LockPosition = false
  MeasureType = 1
  OverTolerance = 0
  References2D = -> [ProjItem002]
  Rotation = 0
  ScaleType = 0
  TheoreticalExact = false
  Type = 5
  UnderTolerance = 0
  X = 2.44528
  Y = 2.98868
FEATURE [TechDraw::DrawViewDimension] Dimension002
  AngleOverride = false
  Arbitrary = false
  ArbitraryTolerances = false
  EqualTolerance = true
  ExtensionAngle = 0
  FormatSpec = %.2w
  FormatSpecOverTolerance = %+.2w
  FormatSpecUnderTolerance = %+.2w
  Inverted = false
  LineAngle = 0
  LockPosition = false
  MeasureType = 1
  OverTolerance = 0
  References2D = -> [ProjItem002]
  Rotation = 0
  ScaleType = 0
  TheoreticalExact = false
  Type = 1
  UnderTolerance = 0
  X = -38.5456
  Y = 32.2226
FEATURE [TechDraw::DrawViewDimension] Dimension003
  AngleOverride = false
  Arbitrary = false
  ArbitraryTolerances = false
  EqualTolerance = true
  ExtensionAngle = 0
  FormatSpec = %.2w
  FormatSpecOverTolerance = %+.2w
  FormatSpecUnderTolerance = %+.2w
  Inverted = false
  LineAngle = 0
  LockPosition = false
  MeasureType = 1
  OverTolerance = 0
  References2D = -> [ProjItem002]
  Rotation = 0
  ScaleType = 0
  TheoreticalExact = false
  Type = 1
  UnderTolerance = 0
  X = -34.6871
  Y = -25.3774
FEATURE [TechDraw::DrawViewDimension] Dimension004
  AngleOverride = false
  Arbitrary = false
  ArbitraryTolerances = false
  EqualTolerance = true
  ExtensionAngle = 0
  FormatSpec = %.2w
  FormatSpecOverTolerance = %+.2w
  FormatSpecUnderTolerance = %+.2w
  Inverted = false
  LineAngle = 0
  LockPosition = false
  MeasureType = 1
  OverTolerance = 0
  References2D = -> [ProjItem]
  Rotation = 0
  ScaleType = 0
  TheoreticalExact = false
  Type = 2
  UnderTolerance = 0
  X = -58.5739
  Y = -17.0651
FEATURE [TechDraw::DrawViewDimension] Dimension005
  AngleOverride = false
  Arbitrary = false
  ArbitraryTolerances = false
  EqualTolerance = true
  ExtensionAngle = 0
  FormatSpec = %.2w
  FormatSpecOverTolerance = %+.2w
  FormatSpecUnderTolerance = %+.2w
  Inverted = false
  LineAngle = 0
  LockPosition = false
  MeasureType = 1
  OverTolerance = 0
  References2D = -> [ProjItem]
  Rotation = 0
  ScaleType = 0
  TheoreticalExact = false
  Type = 1
  UnderTolerance = 0
  X = -29.2305
  Y = -36.6274
FEATURE [TechDraw::DrawViewDimension] Dimension006
  AngleOverride = false
  Arbitrary = false
  ArbitraryTolerances = false
  EqualTolerance = true
  ExtensionAngle = 0
  FormatSpec = %.2w
  FormatSpecOverTolerance = %+.2w
  FormatSpecUnderTolerance = %+.2w
  Inverted = false
  LineAngle = 0
  LockPosition = false
  MeasureType = 1
  OverTolerance = 0
  References2D = -> [ProjItem]
  Rotation = 0
  ScaleType = 0
  TheoreticalExact = false
  Type = 1
  UnderTolerance = 0
  X = -5.45881
  Y = -36.3547
FEATURE [TechDraw::DrawViewDimension] Dimension007
  AngleOverride = false
  Arbitrary = false
  ArbitraryTolerances = false
  EqualTolerance = true
  ExtensionAngle = 0
  FormatSpec = %.2w
  FormatSpecOverTolerance = %+.2w
  FormatSpecUnderTolerance = %+.2w
  Inverted = false
  LineAngle = 0
  LockPosition = false
  MeasureType = 1
  OverTolerance = 0
  References2D = -> [ProjItem]
  Rotation = 0
  ScaleType = 0
  TheoreticalExact = false
  Type = 2
  UnderTolerance = 0
  X = 12.3657
  Y = -7
FEATURE [TechDraw::DrawViewAnnotation] Annotation
  Font = osifont
  LineSpace = 80
  LockPosition = false
  MaxWidth = -1
  Rotation = 0
  ScaleType = 0
  Text = 1. Rodhole bohren | 2. Lever Aussparung fräsen (beidseitig) | 3. Frontrundung schleifen | 4. Front Aussparung fräsen
  TextSize = 5
  TextStyle = 0
  X = 223.76
  Y = 146.57
FEATURE [TechDraw::DrawViewAnnotation] Annotation001
  Font = osifont
  LineSpace = 80
  LockPosition = false
  MaxWidth = -1
  Rotation = 0
  ScaleType = 0
  Text = Mit Stufenbohrer testen
  TextSize = 5
  TextStyle = 0
  X = 126.221
  Y = 175.37
FEATURE [TechDraw::DrawViewAnnotation] Annotation002
  Font = osifont
  LineSpace = 80
  LockPosition = false
  MaxWidth = -1
  Rotation = 0
  ScaleType = 0
  Text = Armrest Body
  TextSize = 15
  TextStyle = 0
  X = 224.304
  Y = 185.966
FEATURE [TechDraw::DrawPage] Page  label="bodyPlan"
  KeepUpdated = true
  NextBalloonIndex = 1
  ProjectionType = 0
  Template = -> Template
  Views = -> [ProjGroup,Dimension,Dimension001,Dimension002,Dimension003,Dimension004,Dimension005,Dimension006,Dimension007,Annotation,Annotation001,Annotation002]
FEATURE [TechDraw::DrawSVGTemplate] Template001
  EditableTexts = Designed_by_Name=Michi Hirczy; FC-Date=2023-12-08; FC-Title=Lever Block Parts
  Height = 210
  Orientation = 1
  Width = 297
FEATURE [TechDraw::DrawProjGroupItem] ProjItem003  label="Front001"
  CoarseView = false
  Direction = (0,1,0)
  Focus = 100
  HardHidden = false
  IsoCount = 0
  IsoHidden = false
  IsoVisible = false
  LockPosition = true
  Perspective = false
  Rotation = 0
  RotationVector = (-1,0,0)
  ScaleType = 2
  SeamHidden = false
  SeamVisible = true
  SmoothHidden = false
  SmoothVisible = true
  Source = -> [Pad003]
  Type = 0
  X = 0
  XDirection = (-1,0,0)
  Y = 0
FEATURE [TechDraw::DrawProjGroup] ProjGroup001  label="LeverPin"
  Anchor = -> ProjItem003
  AutoDistribute = true
  LockPosition = false
  ProjectionType = 0
  Rotation = 0
  ScaleType = 0
  Source = -> [Pad003]
  Views = -> [ProjItem003]
  X = 229.255
  Y = 161.792
  spacingX = 15
  spacingY = 15
FEATURE [TechDraw::DrawViewDimension] Dimension008
  AngleOverride = false
  Arbitrary = false
  ArbitraryTolerances = false
  EqualTolerance = true
  ExtensionAngle = 0
  FormatSpec = %.2w
  FormatSpecOverTolerance = %+.2w
  FormatSpecUnderTolerance = %+.2w
  Inverted = false
  LineAngle = 0
  LockPosition = false
  MeasureType = 1
  OverTolerance = 0
  References2D = -> [ProjItem003]
  Rotation = 0
  ScaleType = 0
  TheoreticalExact = false
  Type = 1
  UnderTolerance = 0
  X = -10.2506
  Y = 19.0849
FEATURE [TechDraw::DrawProjGroupItem] ProjItem004  label="Front002"
  CoarseView = false
  Direction = (0,1,0)
  Focus = 100
  HardHidden = false
  IsoCount = 0
  IsoHidden = false
  IsoVisible = false
  LockPosition = true
  Perspective = false
  Rotation = 0
  RotationVector = (-1,0,0)
  ScaleType = 2
  SeamHidden = false
  SeamVisible = true
  SmoothHidden = false
  SmoothVisible = true
  Source = -> [Body005]
  Type = 0
  X = 0
  XDirection = (-1,0,0)
  Y = 0
FEATURE [TechDraw::DrawProjGroupItem] ProjItem007  label="Right"
  CoarseView = false
  Direction = (-1,1e-16,0)
  Focus = 100
  HardHidden = true
  IsoCount = 0
  IsoHidden = true
  IsoVisible = false
  LockPosition = true
  Perspective = false
  Rotation = 0
  RotationVector = (1,0,0)
  ScaleType = 2
  SeamHidden = false
  SeamVisible = true
  SmoothHidden = true
  SmoothVisible = true
  Source = -> [Body005]
  Type = 2
  X = -46.7925
  XDirection = (-1e-16,-1,0)
  Y = 0
FEATURE [TechDraw::DrawProjGroup] ProjGroup002  label="PinBlock001"
  Anchor = -> ProjItem004
  AutoDistribute = true
  LockPosition = false
  ProjectionType = 0
  Rotation = 0
  ScaleType = 0
  Source = -> [Body005]
  Views = -> [ProjItem004,ProjItem007]
  X = 100.764
  Y = 147.453
  spacingX = 15
  spacingY = 15
FEATURE [TechDraw::DrawViewDimension] Dimension009
  AngleOverride = false
  Arbitrary = false
  ArbitraryTolerances = false
  EqualTolerance = true
  ExtensionAngle = 0
  FormatSpec = %.2w
  FormatSpecOverTolerance = %+.2w
  FormatSpecUnderTolerance = %+.2w
  Inverted = false
  LineAngle = 0
  LockPosition = false
  MeasureType = 1
  OverTolerance = 0
  References2D = -> [ProjItem004]
  Rotation = 0
  ScaleType = 0
  TheoreticalExact = false
  Type = 1
  UnderTolerance = 0
  X = -0.754717
  Y = 33.2453
FEATURE [TechDraw::DrawViewDimension] Dimension010
  AngleOverride = false
  Arbitrary = false
  ArbitraryTolerances = false
  EqualTolerance = true
  ExtensionAngle = 0
  FormatSpec = %.2w
  FormatSpecOverTolerance = %+.2w
  FormatSpecUnderTolerance = %+.2w
  Inverted = false
  LineAngle = 0
  LockPosition = false
  MeasureType = 1
  OverTolerance = 0
  References2D = -> [ProjItem007]
  Rotation = 0
  ScaleType = 0
  TheoreticalExact = false
  Type = 1
  UnderTolerance = 0
  X = 0.566038
  Y = 34.7547
FEATURE [TechDraw::DrawViewDimension] Dimension011
  AngleOverride = false
  Arbitrary = false
  ArbitraryTolerances = false
  EqualTolerance = true
  ExtensionAngle = 0
  FormatSpec = %.2w
  FormatSpecOverTolerance = %+.2w
  FormatSpecUnderTolerance = %+.2w
  Inverted = false
  LineAngle = 0
  LockPosition = false
  MeasureType = 1
  OverTolerance = 0
  References2D = -> [ProjItem007]
  Rotation = 0
  ScaleType = 0
  TheoreticalExact = false
  Type = 2
  UnderTolerance = 0
  X = -33.3868
  Y = 5.89623
FEATURE [TechDraw::DrawViewDimension] Dimension012
  AngleOverride = false
  Arbitrary = false
  ArbitraryTolerances = false
  EqualTolerance = true
  ExtensionAngle = 0
  FormatSpec = %.2w
  FormatSpecOverTolerance = %+.2w
  FormatSpecUnderTolerance = %+.2w
  Inverted = false
  LineAngle = 0
  LockPosition = false
  MeasureType = 1
  OverTolerance = 0
  References2D = -> [ProjItem007]
  Rotation = 0
  ScaleType = 0
  TheoreticalExact = false
  Type = 1
  UnderTolerance = 0
  X = -6.62264
  Y = 24.6085
FEATURE [TechDraw::DrawViewDimension] Dimension013
  AngleOverride = false
  Arbitrary = false
  ArbitraryTolerances = false
  EqualTolerance = true
  ExtensionAngle = 0
  FormatSpec = ⌀%.2w
  FormatSpecOverTolerance = %+.2w
  FormatSpecUnderTolerance = %+.2w
  Inverted = false
  LineAngle = 0
  LockPosition = false
  MeasureType = 1
  OverTolerance = 0
  References2D = -> [ProjItem007]
  Rotation = 0
  ScaleType = 0
  TheoreticalExact = false
  Type = 5
  UnderTolerance = 0
  X = 7.16981
  Y = 6.22642
FEATURE [TechDraw::DrawViewDimension] Dimension014
  AngleOverride = false
  Arbitrary = false
  ArbitraryTolerances = false
  EqualTolerance = true
  ExtensionAngle = 0
  FormatSpec = ⌀%.2w
  FormatSpecOverTolerance = %+.2w
  FormatSpecUnderTolerance = %+.2w
  Inverted = false
  LineAngle = 0
  LockPosition = false
  MeasureType = 1
  OverTolerance = 0
  References2D = -> [ProjItem004]
  Rotation = 0
  ScaleType = 0
  TheoreticalExact = false
  Type = 5
  UnderTolerance = 0
  X = -20.7547
  Y = -4.90566
FEATURE [TechDraw::DrawViewDimension] Dimension015
  AngleOverride = false
  Arbitrary = false
  ArbitraryTolerances = false
  EqualTolerance = true
  ExtensionAngle = 0
  FormatSpec = %.2w
  FormatSpecOverTolerance = %+.2w
  FormatSpecUnderTolerance = %+.2w
  Inverted = false
  LineAngle = 0
  LockPosition = false
  MeasureType = 1
  OverTolerance = 0
  References2D = -> [ProjItem004]
  Rotation = 0
  ScaleType = 0
  TheoreticalExact = false
  Type = 2
  UnderTolerance = 0
  X = 18.9575
  Y = -14.7472
FEATURE [TechDraw::DrawViewDimension] Dimension016
  AngleOverride = false
  Arbitrary = false
  ArbitraryTolerances = false
  EqualTolerance = true
  ExtensionAngle = 0
  FormatSpec = %.2w
  FormatSpecOverTolerance = %+.2w
  FormatSpecUnderTolerance = %+.2w
  Inverted = false
  LineAngle = 0
  LockPosition = false
  MeasureType = 1
  OverTolerance = 0
  References2D = -> [ProjItem004]
  Rotation = 0
  ScaleType = 0
  TheoreticalExact = false
  Type = 2
  UnderTolerance = 0
  X = 31.7877
  Y = -1.13207
FEATURE [TechDraw::DrawViewDimension] Dimension017
  AngleOverride = false
  Arbitrary = false
  ArbitraryTolerances = false
  EqualTolerance = true
  ExtensionAngle = 0
  FormatSpec = %.2w
  FormatSpecOverTolerance = %+.2w
  FormatSpecUnderTolerance = %+.2w
  Inverted = false
  LineAngle = 0
  LockPosition = false
  MeasureType = 1
  OverTolerance = 0
  References2D = -> [ProjItem004]
  Rotation = 0
  ScaleType = 0
  TheoreticalExact = false
  Type = 2
  UnderTolerance = 0
  X = 19.0566
  Y = 2.61132
FEATURE [TechDraw::DrawViewDimension] Dimension018
  AngleOverride = false
  Arbitrary = false
  ArbitraryTolerances = false
  EqualTolerance = true
  ExtensionAngle = 0
  FormatSpec = ⌀%.2w
  FormatSpecOverTolerance = %+.2w
  FormatSpecUnderTolerance = %+.2w
  Inverted = false
  LineAngle = 0
  LockPosition = false
  MeasureType = 1
  OverTolerance = 0
  References2D = -> [ProjItem004]
  Rotation = 0
  ScaleType = 0
  TheoreticalExact = false
  Type = 5
  UnderTolerance = 0
  X = -21.1321
  Y = 9.43396
FEATURE [TechDraw::DrawViewDimension] Dimension019
  AngleOverride = false
  Arbitrary = false
  ArbitraryTolerances = false
  EqualTolerance = true
  ExtensionAngle = 0
  FormatSpec = %.2w
  FormatSpecOverTolerance = %+.2w
  FormatSpecUnderTolerance = %+.2w
  Inverted = false
  LineAngle = 0
  LockPosition = false
  MeasureType = 1
  OverTolerance = 0
  References2D = -> [ProjItem003]
  Rotation = 0
  ScaleType = 0
  TheoreticalExact = false
  Type = 2
  UnderTolerance = 0
  X = -45.043
  Y = 1.93396
FEATURE [TechDraw::DrawViewDimension] Dimension020
  AngleOverride = false
  Arbitrary = false
  ArbitraryTolerances = false
  EqualTolerance = true
  ExtensionAngle = 0
  FormatSpec = %.2w
  FormatSpecOverTolerance = %+.2w
  FormatSpecUnderTolerance = %+.2w
  Inverted = false
  LineAngle = 0
  LockPosition = false
  MeasureType = 1
  OverTolerance = 0
  References2D = -> [ProjItem003]
  Rotation = 0
  ScaleType = 0
  TheoreticalExact = false
  Type = 1
  UnderTolerance = 0
  X = 18.1902
  Y = 19.0052
FEATURE [TechDraw::DrawProjGroupItem] ProjItem008  label="Front003"
  CoarseView = false
  Direction = (-1,0,0)
  Focus = 100
  HardHidden = false
  IsoCount = 0
  IsoHidden = false
  IsoVisible = false
  LockPosition = true
  Perspective = false
  Rotation = 0
  RotationVector = (0,-1,0)
  ScaleType = 2
  SeamHidden = false
  SeamVisible = true
  SmoothHidden = false
  SmoothVisible = true
  Source = -> [Body004]
  Type = 0
  X = 0
  XDirection = (0,-1,0)
  Y = 0
FEATURE [TechDraw::DrawProjGroupItem] ProjItem009  label="Left"
  CoarseView = false
  Direction = (-1e-16,1,0)
  Focus = 100
  HardHidden = false
  IsoCount = 0
  IsoHidden = false
  IsoVisible = false
  LockPosition = false
  Perspective = false
  Rotation = 0
  RotationVector = (1,0,0)
  ScaleType = 2
  SeamHidden = false
  SeamVisible = true
  SmoothHidden = false
  SmoothVisible = true
  Source = -> [Body004]
  Type = 1
  X = 40.5
  XDirection = (-1,-1e-16,0)
  Y = 0
FEATURE [TechDraw::DrawProjGroup] ProjGroup003  label="LockingPin001"
  Anchor = -> ProjItem008
  AutoDistribute = true
  LockPosition = false
  ProjectionType = 0
  Rotation = 0
  ScaleType = 2
  Source = -> [Body004]
  Views = -> [ProjItem008,ProjItem009]
  X = 57.9454
  Y = 83.4748
  spacingX = 15
  spacingY = 15
FEATURE [TechDraw::DrawViewDimension] Dimension021
  AngleOverride = false
  Arbitrary = false
  ArbitraryTolerances = false
  EqualTolerance = true
  ExtensionAngle = 0
  FormatSpec = ⌀%.2w
  FormatSpecOverTolerance = %+.2w
  FormatSpecUnderTolerance = %+.2w
  Inverted = false
  LineAngle = 0
  LockPosition = false
  MeasureType = 1
  OverTolerance = 0
  References2D = -> [ProjItem009]
  Rotation = 0
  ScaleType = 0
  TheoreticalExact = false
  Type = 5
  UnderTolerance = 0
  X = 8.61199
  Y = 5.26288
FEATURE [TechDraw::DrawViewDimension] Dimension022
  AngleOverride = false
  Arbitrary = false
  ArbitraryTolerances = false
  EqualTolerance = true
  ExtensionAngle = 0
  FormatSpec = %.2w
  FormatSpecOverTolerance = %+.2w
  FormatSpecUnderTolerance = %+.2w
  Inverted = false
  LineAngle = 0
  LockPosition = false
  MeasureType = 1
  OverTolerance = 0
  References2D = -> [ProjItem008]
  Rotation = 0
  ScaleType = 0
  TheoreticalExact = false
  Type = 2
  UnderTolerance = 0
  X = 18.2524
  Y = 2.61961
FEATURE [TechDraw::DrawViewDimension] Dimension023
  AngleOverride = false
  Arbitrary = false
  ArbitraryTolerances = false
  EqualTolerance = true
  ExtensionAngle = 0
  FormatSpec = %.2w
  FormatSpecOverTolerance = %+.2w
  FormatSpecUnderTolerance = %+.2w
  Inverted = false
  LineAngle = 0
  LockPosition = false
  MeasureType = 1
  OverTolerance = 0
  References2D = -> [ProjItem008]
  Rotation = 0
  ScaleType = 0
  TheoreticalExact = false
  Type = 2
  UnderTolerance = 0
  X = -27.103
  Y = 2.14117
FEATURE [TechDraw::DrawViewDimension] Dimension024
  AngleOverride = false
  Arbitrary = false
  ArbitraryTolerances = false
  EqualTolerance = true
  ExtensionAngle = 0
  FormatSpec = %.2w
  FormatSpecOverTolerance = %+.2w
  FormatSpecUnderTolerance = %+.2w
  Inverted = false
  LineAngle = 0
  LockPosition = false
  MeasureType = 1
  OverTolerance = 0
  References2D = -> [ProjItem008]
  Rotation = 0
  ScaleType = 0
  TheoreticalExact = false
  Type = 1
  UnderTolerance = 0
  X = -5.35856
  Y = 16.0314
FEATURE [TechDraw::DrawViewDimension] Dimension025
  AngleOverride = false
  Arbitrary = false
  ArbitraryTolerances = false
  EqualTolerance = true
  ExtensionAngle = 0
  FormatSpec = %.2w
  FormatSpecOverTolerance = %+.2w
  FormatSpecUnderTolerance = %+.2w
  Inverted = false
  LineAngle = 0
  LockPosition = false
  MeasureType = 1
  OverTolerance = 0
  References2D = -> [ProjItem008]
  Rotation = 0
  ScaleType = 0
  TheoreticalExact = false
  Type = 1
  UnderTolerance = 0
  X = 7.03261
  Y = 16.1135
FEATURE [TechDraw::DrawViewDimension] Dimension026
  AngleOverride = false
  Arbitrary = false
  ArbitraryTolerances = false
  EqualTolerance = true
  ExtensionAngle = 0
  FormatSpec = %.2w
  FormatSpecOverTolerance = %+.2w
  FormatSpecUnderTolerance = %+.2w
  Inverted = false
  LineAngle = 0
  LockPosition = false
  MeasureType = 1
  OverTolerance = 0
  References2D = -> [ProjItem008]
  Rotation = 0
  ScaleType = 0
  TheoreticalExact = false
  Type = 1
  UnderTolerance = 0
  X = 0.000273
  Y = -8.28032
FEATURE [TechDraw::DrawViewDimension] Dimension027
  AngleOverride = false
  Arbitrary = false
  ArbitraryTolerances = false
  EqualTolerance = true
  ExtensionAngle = 0
  FormatSpec = %.2w
  FormatSpecOverTolerance = %+.2w
  FormatSpecUnderTolerance = %+.2w
  Inverted = false
  LineAngle = 0
  LockPosition = false
  MeasureType = 1
  OverTolerance = 0
  References2D = -> [ProjItem007]
  Rotation = 0
  ScaleType = 0
  TheoreticalExact = false
  Type = 2
  UnderTolerance = 0
  X = -21.0615
  Y = -2.3888
FEATURE [TechDraw::DrawPage] Page001  label="leverParts"
  KeepUpdated = true
  NextBalloonIndex = 1
  ProjectionType = 0
  Template = -> Template001
  Views = -> [ProjGroup001,Dimension008,ProjGroup002,Dimension009,Dimension010,Dimension011,Dimension012,Dimension013,Dimension014,Dimension015,Dimension016,Dimension017,Dimension018,Dimension019,Dimension020,ProjGroup003,Dimension021,Dimension022,Dimension023,Dimension024,Dimension025,Dimension026,Dimension027]
FEATURE [TechDraw::DrawSVGTemplate] Template002
  EditableTexts = Designed_by_Name=Michi Hirczy; FC-Date=2023-12-08; FC-Title=Rod
  Height = 210
  Orientation = 1
  Width = 297
FEATURE [TechDraw::DrawProjGroupItem] ProjItem010  label="Front004"
  CoarseView = false
  Direction = (0,-1,0)
  Focus = 100
  HardHidden = false
  IsoCount = 0
  IsoHidden = false
  IsoVisible = false
  LockPosition = true
  Perspective = false
  Rotation = 0
  RotationVector = (0,0,-1)
  ScaleType = 2
  SeamHidden = false
  SeamVisible = true
  SmoothHidden = false
  SmoothVisible = true
  Source = -> [Body]
  Type = 0
  X = 0
  XDirection = (0,0,-1)
  Y = 0
FEATURE [TechDraw::DrawProjGroupItem] ProjItem011  label="Left001"
  CoarseView = false
  Direction = (0,-1e-16,1)
  Focus = 100
  HardHidden = false
  IsoCount = 0
  IsoHidden = false
  IsoVisible = false
  LockPosition = false
  Perspective = false
  Rotation = 0
  RotationVector = (1,0,0)
  ScaleType = 2
  SeamHidden = false
  SeamVisible = true
  SmoothHidden = false
  SmoothVisible = true
  Source = -> [Body]
  Type = 1
  X = 127.483
  XDirection = (0,-1,-1e-16)
  Y = 0
FEATURE [TechDraw::DrawProjGroup] ProjGroup004
  Anchor = -> ProjItem010
  AutoDistribute = false
  LockPosition = false
  ProjectionType = 0
  Rotation = 0
  ScaleType = 0
  Source = -> [Body]
  Views = -> [ProjItem010,ProjItem011]
  X = 113.902
  Y = 112.231
  spacingX = 15
  spacingY = 15
FEATURE [TechDraw::DrawViewDimExtent] DimExtent
  AngleOverride = false
  Arbitrary = false
  ArbitraryTolerances = false
  CosmeticTags = e0900858-99bc-408c-b565-e480386d4d8a | 9f74cb01-cbc2-4233-9d1d-2b97bb20a20f
  DirExtent = 0
  EqualTolerance = true
  ExtensionAngle = 0
  FormatSpec = %.2w
  FormatSpecOverTolerance = %+.2w
  FormatSpecUnderTolerance = %+.2w
  Inverted = false
  LineAngle = 0
  LockPosition = false
  MeasureType = 1
  OverTolerance = 0
  References2D = -> [ProjItem011]
  Rotation = 0
  ScaleType = 0
  Source = -> [ProjItem011]
  TheoreticalExact = false
  Type = 1
  UnderTolerance = 0
  X = 0
  Y = 0
FEATURE [TechDraw::DrawViewDimension] Dimension028
  AngleOverride = false
  Arbitrary = false
  ArbitraryTolerances = false
  EqualTolerance = true
  ExtensionAngle = 0
  FormatSpec = %.2w
  FormatSpecOverTolerance = %+.2w
  FormatSpecUnderTolerance = %+.2w
  Inverted = false
  LineAngle = 0
  LockPosition = false
  MeasureType = 1
  OverTolerance = 0
  References2D = -> [ProjItem011]
  Rotation = 0
  ScaleType = 0
  TheoreticalExact = false
  Type = 1
  UnderTolerance = 0
  X = -1.92925
  Y = 21.1547
FEATURE [TechDraw::DrawViewDimension] Dimension029
  AngleOverride = false
  Arbitrary = false
  ArbitraryTolerances = false
  EqualTolerance = true
  ExtensionAngle = 0
  FormatSpec = %.2w
  FormatSpecOverTolerance = %+.2w
  FormatSpecUnderTolerance = %+.2w
  Inverted = false
  LineAngle = 0
  LockPosition = false
  MeasureType = 1
  OverTolerance = 0
  References2D = -> [ProjItem011]
  Rotation = 0
  ScaleType = 0
  TheoreticalExact = false
  Type = 2
  UnderTolerance = 0
  X = 22.2535
  Y = 16.0849
FEATURE [TechDraw::DrawViewDimension] Dimension030
  AngleOverride = false
  Arbitrary = false
  ArbitraryTolerances = false
  EqualTolerance = true
  ExtensionAngle = 0
  FormatSpec = %.2w
  FormatSpecOverTolerance = %+.2w
  FormatSpecUnderTolerance = %+.2w
  Inverted = false
  LineAngle = 0
  LockPosition = false
  MeasureType = 1
  OverTolerance = 0
  References2D = -> [ProjItem010]
  Rotation = 0
  ScaleType = 0
  TheoreticalExact = false
  Type = 1
  UnderTolerance = 0
  X = 92.1547
  Y = -15.324
FEATURE [TechDraw::DrawViewDimension] Dimension031
  AngleOverride = false
  Arbitrary = false
  ArbitraryTolerances = false
  EqualTolerance = true
  ExtensionAngle = 0
  FormatSpec = ⌀%.2w
  FormatSpecOverTolerance = %+.2w
  FormatSpecUnderTolerance = %+.2w
  Inverted = false
  LineAngle = 0
  LockPosition = false
  MeasureType = 1
  OverTolerance = 0
  References2D = -> [ProjItem010]
  Rotation = 0
  ScaleType = 0
  TheoreticalExact = false
  Type = 5
  UnderTolerance = 0
  X = 95.928
  Y = 2.99027
FEATURE [TechDraw::DrawViewDimension] Dimension032
  AngleOverride = false
  Arbitrary = false
  ArbitraryTolerances = false
  EqualTolerance = true
  ExtensionAngle = 0
  FormatSpec = %.2w
  FormatSpecOverTolerance = %+.2w
  FormatSpecUnderTolerance = %+.2w
  Inverted = false
  LineAngle = 0
  LockPosition = false
  MeasureType = 1
  OverTolerance = 0
  References2D = -> [ProjItem010]
  Rotation = 0
  ScaleType = 0
  TheoreticalExact = false
  Type = 1
  UnderTolerance = 0
  X = 78.369
  Y = -15.4507
FEATURE [TechDraw::DrawViewDimension] Dimension033
  AngleOverride = false
  Arbitrary = false
  ArbitraryTolerances = false
  EqualTolerance = true
  ExtensionAngle = 0
  FormatSpec = %.2w
  FormatSpecOverTolerance = %+.2w
  FormatSpecUnderTolerance = %+.2w
  Inverted = false
  LineAngle = 0
  LockPosition = false
  MeasureType = 1
  OverTolerance = 0
  References2D = -> [ProjItem010]
  Rotation = 0
  ScaleType = 0
  TheoreticalExact = false
  Type = 1
  UnderTolerance = 0
  X = 66.519
  Y = -15.7128
FEATURE [TechDraw::DrawViewDimension] Dimension034
  AngleOverride = false
  Arbitrary = false
  ArbitraryTolerances = false
  EqualTolerance = true
  ExtensionAngle = 0
  FormatSpec = ⌀%.2w
  FormatSpecOverTolerance = %+.2w
  FormatSpecUnderTolerance = %+.2w
  Inverted = false
  LineAngle = 0
  LockPosition = false
  MeasureType = 1
  OverTolerance = 0
  References2D = -> [ProjItem010]
  Rotation = 0
  ScaleType = 0
  TheoreticalExact = false
  Type = 5
  UnderTolerance = 0
  X = 50.0524
  Y = -11.3994
FEATURE [TechDraw::DrawViewDimension] Dimension035
  AngleOverride = false
  Arbitrary = false
  ArbitraryTolerances = false
  EqualTolerance = true
  ExtensionAngle = 0
  FormatSpec = %.2w
  FormatSpecOverTolerance = %+.2w
  FormatSpecUnderTolerance = %+.2w
  Inverted = false
  LineAngle = 0
  LockPosition = false
  MeasureType = 1
  OverTolerance = 0
  References2D = -> [ProjItem010]
  Rotation = 0
  ScaleType = 0
  TheoreticalExact = false
  Type = 1
  UnderTolerance = 0
  X = 81.631
  Y = 17.3994
FEATURE [TechDraw::DrawViewDimension] Dimension036
  AngleOverride = false
  Arbitrary = false
  ArbitraryTolerances = false
  EqualTolerance = true
  ExtensionAngle = 0
  FormatSpec = %.2w
  FormatSpecOverTolerance = %+.2w
  FormatSpecUnderTolerance = %+.2w
  Inverted = false
  LineAngle = 0
  LockPosition = false
  MeasureType = 1
  OverTolerance = 0
  References2D = -> [ProjItem010]
  Rotation = 0
  ScaleType = 0
  TheoreticalExact = false
  Type = 1
  UnderTolerance = 0
  X = 75.5431
  Y = 22.9025
FEATURE [TechDraw::DrawViewDimension] Dimension037
  AngleOverride = false
  Arbitrary = false
  ArbitraryTolerances = false
  EqualTolerance = true
  ExtensionAngle = 0
  FormatSpec = %.2w
  FormatSpecOverTolerance = %+.2w
  FormatSpecUnderTolerance = %+.2w
  Inverted = false
  LineAngle = 0
  LockPosition = false
  MeasureType = 1
  OverTolerance = 0
  References2D = -> [ProjItem010]
  Rotation = 0
  ScaleType = 0
  TheoreticalExact = false
  Type = 1
  UnderTolerance = 0
  X = 69.4551
  Y = 29.3229
FEATURE [TechDraw::DrawViewDimension] Dimension038
  AngleOverride = false
  Arbitrary = false
  ArbitraryTolerances = false
  EqualTolerance = true
  ExtensionAngle = 0
  FormatSpec = %.2w
  FormatSpecOverTolerance = %+.2w
  FormatSpecUnderTolerance = %+.2w
  Inverted = false
  LineAngle = 0
  LockPosition = false
  MeasureType = 1
  OverTolerance = 0
  References2D = -> [ProjItem010]
  Rotation = 0
  ScaleType = 0
  TheoreticalExact = false
  Type = 1
  UnderTolerance = 0
  X = 61.2708
  Y = 35.088
FEATURE [TechDraw::DrawViewDimension] Dimension039
  AngleOverride = false
  Arbitrary = false
  ArbitraryTolerances = false
  EqualTolerance = true
  ExtensionAngle = 0
  FormatSpec = %.2w
  FormatSpecOverTolerance = %+.2w
  FormatSpecUnderTolerance = %+.2w
  Inverted = false
  LineAngle = 0
  LockPosition = false
  MeasureType = 1
  OverTolerance = 0
  References2D = -> [ProjItem010]
  Rotation = 0
  ScaleType = 0
  TheoreticalExact = false
  Type = 1
  UnderTolerance = 0
  X = 54.0036
  Y = 41.5084
FEATURE [TechDraw::DrawViewDimension] Dimension040
  AngleOverride = false
  Arbitrary = false
  ArbitraryTolerances = false
  EqualTolerance = true
  ExtensionAngle = 0
  FormatSpec = %.2w
  FormatSpecOverTolerance = %+.2w
  FormatSpecUnderTolerance = %+.2w
  Inverted = false
  LineAngle = 0
  LockPosition = false
  MeasureType = 1
  OverTolerance = 0
  References2D = -> [ProjItem010]
  Rotation = 0
  ScaleType = 0
  TheoreticalExact = false
  Type = 1
  UnderTolerance = 0
  X = 45.9764
  Y = 48.6415
FEATURE [TechDraw::DrawViewDimension] Dimension041
  AngleOverride = false
  Arbitrary = false
  ArbitraryTolerances = false
  EqualTolerance = true
  ExtensionAngle = 0
  FormatSpec = %.2w
  FormatSpecOverTolerance = %+.2w
  FormatSpecUnderTolerance = %+.2w
  Inverted = false
  LineAngle = 0
  LockPosition = false
  MeasureType = 1
  OverTolerance = 0
  References2D = -> [ProjItem010]
  Rotation = 0
  ScaleType = 0
  TheoreticalExact = false
  Type = 1
  UnderTolerance = 0
  X = 37.7396
  Y = 55.0566
FEATURE [TechDraw::DrawViewDimension] Dimension042
  AngleOverride = false
  Arbitrary = false
  ArbitraryTolerances = false
  EqualTolerance = true
  ExtensionAngle = 0
  FormatSpec = %.2w
  FormatSpecOverTolerance = %+.2w
  FormatSpecUnderTolerance = %+.2w
  Inverted = false
  LineAngle = 0
  LockPosition = false
  MeasureType = 1
  OverTolerance = 0
  References2D = -> [ProjItem010]
  Rotation = 0
  ScaleType = 0
  TheoreticalExact = false
  Type = 1
  UnderTolerance = 0
  X = 29.6915
  Y = 61.8491
FEATURE [TechDraw::DrawViewDimension] Dimension043
  AngleOverride = false
  Arbitrary = false
  ArbitraryTolerances = false
  EqualTolerance = true
  ExtensionAngle = 0
  FormatSpec = %.2w
  FormatSpecOverTolerance = %+.2w
  FormatSpecUnderTolerance = %+.2w
  Inverted = false
  LineAngle = 0
  LockPosition = false
  MeasureType = 1
  OverTolerance = 0
  References2D = -> [ProjItem010]
  Rotation = 0
  ScaleType = 0
  TheoreticalExact = false
  Type = 1
  UnderTolerance = 0
  X = 20.134
  Y = 68.4528
FEATURE [TechDraw::DrawViewDimension] Dimension044
  AngleOverride = false
  Arbitrary = false
  ArbitraryTolerances = false
  EqualTolerance = true
  ExtensionAngle = 0
  FormatSpec = %.2w
  FormatSpecOverTolerance = %+.2w
  FormatSpecUnderTolerance = %+.2w
  Inverted = false
  LineAngle = 0
  LockPosition = false
  MeasureType = 1
  OverTolerance = 0
  References2D = -> [ProjItem010]
  Rotation = 0
  ScaleType = 0
  TheoreticalExact = false
  Type = 1
  UnderTolerance = 0
  X = 9.8217
  Y = 75.2453
FEATURE [TechDraw::DrawProjGroupItem] ProjItem012  label="Front005"
  CoarseView = false
  Direction = (0,-1,0)
  Focus = 100
  HardHidden = false
  IsoCount = 0
  IsoHidden = false
  IsoVisible = false
  LockPosition = true
  Perspective = false
  Rotation = 0
  RotationVector = (0,0,-1)
  ScaleType = 2
  SeamHidden = false
  SeamVisible = true
  SmoothHidden = false
  SmoothVisible = true
  Source = -> [Body003]
  Type = 0
  X = 0
  XDirection = (0,0,-1)
  Y = 0
FEATURE [TechDraw::DrawProjGroupItem] ProjItem013  label="Right001"
  CoarseView = false
  Direction = (0,-1e-16,-1)
  Focus = 100
  HardHidden = false
  IsoCount = 0
  IsoHidden = false
  IsoVisible = false
  LockPosition = false
  Perspective = false
  Rotation = 0
  RotationVector = (1,0,0)
  ScaleType = 2
  SeamHidden = false
  SeamVisible = true
  SmoothHidden = false
  SmoothVisible = true
  Source = -> [Body003]
  Type = 2
  X = -23.4
  XDirection = (0,1,-1e-16)
  Y = 0
FEATURE [TechDraw::DrawProjGroup] ProjGroup005
  Anchor = -> ProjItem012
  AutoDistribute = true
  LockPosition = false
  ProjectionType = 0
  Rotation = 0
  ScaleType = 0
  Source = -> [Body003]
  Views = -> [ProjItem012,ProjItem013]
  X = 93.3453
  Y = 44.683
  spacingX = 15
  spacingY = 15
FEATURE [TechDraw::DrawViewDimension] Dimension045
  AngleOverride = false
  Arbitrary = false
  ArbitraryTolerances = false
  EqualTolerance = true
  ExtensionAngle = 0
  FormatSpec = %.2w
  FormatSpecOverTolerance = %+.2w
  FormatSpecUnderTolerance = %+.2w
  Inverted = false
  LineAngle = 0
  LockPosition = false
  MeasureType = 1
  OverTolerance = 0
  References2D = -> [ProjItem012]
  Rotation = 0
  ScaleType = 0
  TheoreticalExact = false
  Type = 1
  UnderTolerance = 0
  X = -0.206688
  Y = 12.9006
FEATURE [TechDraw::DrawViewDimension] Dimension046
  AngleOverride = false
  Arbitrary = false
  ArbitraryTolerances = false
  EqualTolerance = true
  ExtensionAngle = 0
  FormatSpec = ⌀%.2w
  FormatSpecOverTolerance = %+.2w
  FormatSpecUnderTolerance = %+.2w
  Inverted = false
  LineAngle = 0
  LockPosition = false
  MeasureType = 1
  OverTolerance = 0
  References2D = -> [ProjItem013]
  Rotation = 0
  ScaleType = 0
  TheoreticalExact = false
  Type = 5
  UnderTolerance = 0
  X = 9.92101
  Y = 2.89363
FEATURE [TechDraw::DrawViewDimension] Dimension047
  AngleOverride = false
  Arbitrary = false
  ArbitraryTolerances = false
  EqualTolerance = true
  ExtensionAngle = 0
  FormatSpec = ⌀%.2w
  FormatSpecOverTolerance = %+.2w
  FormatSpecUnderTolerance = %+.2w
  Inverted = false
  LineAngle = 0
  LockPosition = false
  MeasureType = 1
  OverTolerance = 0
  References2D = -> [ProjItem013]
  Rotation = 0
  ScaleType = 0
  TheoreticalExact = false
  Type = 5
  UnderTolerance = 0
  X = -17.9818
  Y = 0.620063
FEATURE [TechDraw::DrawPage] Page002  label="Rod001"
  KeepUpdated = true
  NextBalloonIndex = 1
  ProjectionType = 0
  Template = -> Template002
  Views = -> [ProjGroup004,Dimension028,Dimension029,Dimension030,Dimension031,Dimension032,Dimension033,Dimension034,Dimension035,Dimension036,Dimension037,Dimension038,Dimension039,Dimension040,Dimension041,Dimension042,Dimension043,Dimension044,ProjGroup005,Dimension045,Dimension046,Dimension047]
